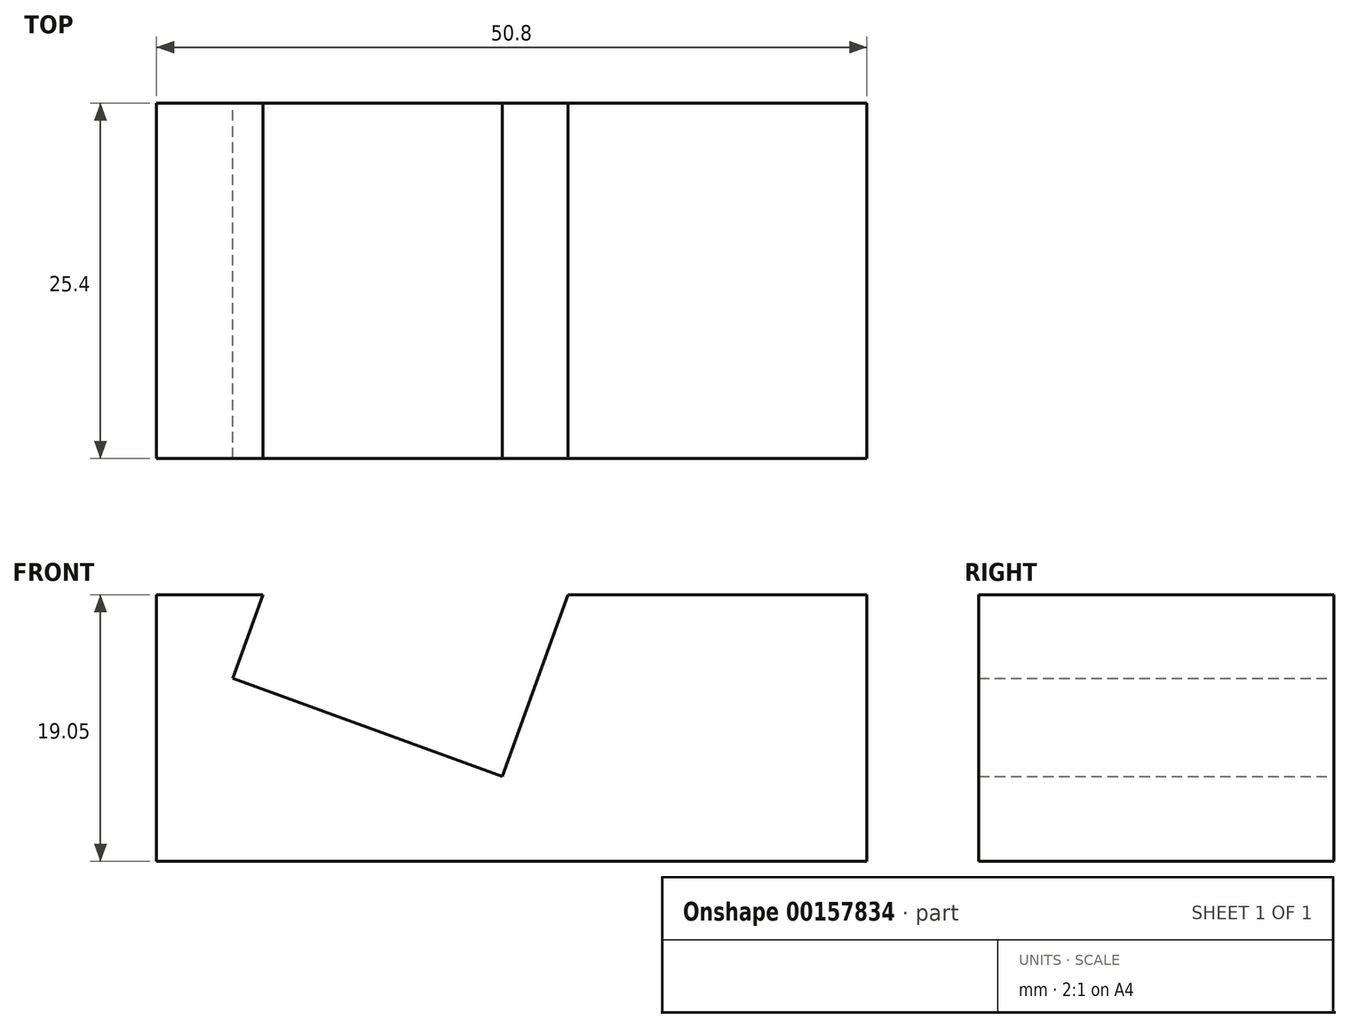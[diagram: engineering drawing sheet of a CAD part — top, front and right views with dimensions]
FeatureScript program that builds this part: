
annotation { "Feature Type Name" : "Feature", "Feature Type Description" : "" }
export const myFeature = defineFeature(function(context is Context, id is Id, definition is map)
    precondition{}
    {
        {
            var Q0;
            Q0=qCreatedBy(makeId("Front.planeOp"),FACE);
            var sketch = newSketch(context, id + "F0", { "sketchPlane" : qUnion([Q0])});
            skLineSegment(sketch, "E0", {"start": v(0, 19.05) * mm, "end": v(0, 0) * mm});
            skLineSegment(sketch, "E1", {"start": v(0, 19.05) * mm, "end": v(7.62, 19.05) * mm});
            skLineSegment(sketch, "E2", {"start": v(7.62, 19.05) * mm, "end": v(7.62, 19.05) * mm});
            skLineSegment(sketch, "E3", {"start": v(7.62, 19.05) * mm, "end": v(5.45, 13.08) * mm});
            skLineSegment(sketch, "E4", {"start": v(5.45, 13.08) * mm, "end": v(5.45, 13.08) * mm});
            skLineSegment(sketch, "E5", {"start": v(5.45, 13.08) * mm, "end": v(24.71, 6.07) * mm});
            skLineSegment(sketch, "E6", {"start": v(24.71, 6.07) * mm, "end": v(24.71, 6.07) * mm});
            skLineSegment(sketch, "E7", {"start": v(29.44, 19.05) * mm, "end": v(24.71, 6.07) * mm});
            skLineSegment(sketch, "E8", {"start": v(7.62, 19.05) * mm, "end": v(29.44, 19.05) * mm, "construction": true});
            skLineSegment(sketch, "E9", {"start": v(29.44, 19.05) * mm, "end": v(50.8, 19.05) * mm});
            skLineSegment(sketch, "E10", {"start": v(50.8, 19.05) * mm, "end": v(50.8, 19.05) * mm});
            skLineSegment(sketch, "E11", {"start": v(50.8, 0) * mm, "end": v(50.8, 19.05) * mm});
            skLineSegment(sketch, "E12", {"start": v(50.8, 0) * mm, "end": v(0, 0) * mm});
            skSolve(sketch);
        }
        {
            var Q0;
            Q0 = qSketchRegion(id + "F0", true);
            extrude(context, id + "F1", {"entities" : qUnion([Q0]), "depth" : 25.4 * mm});
        }
    });
